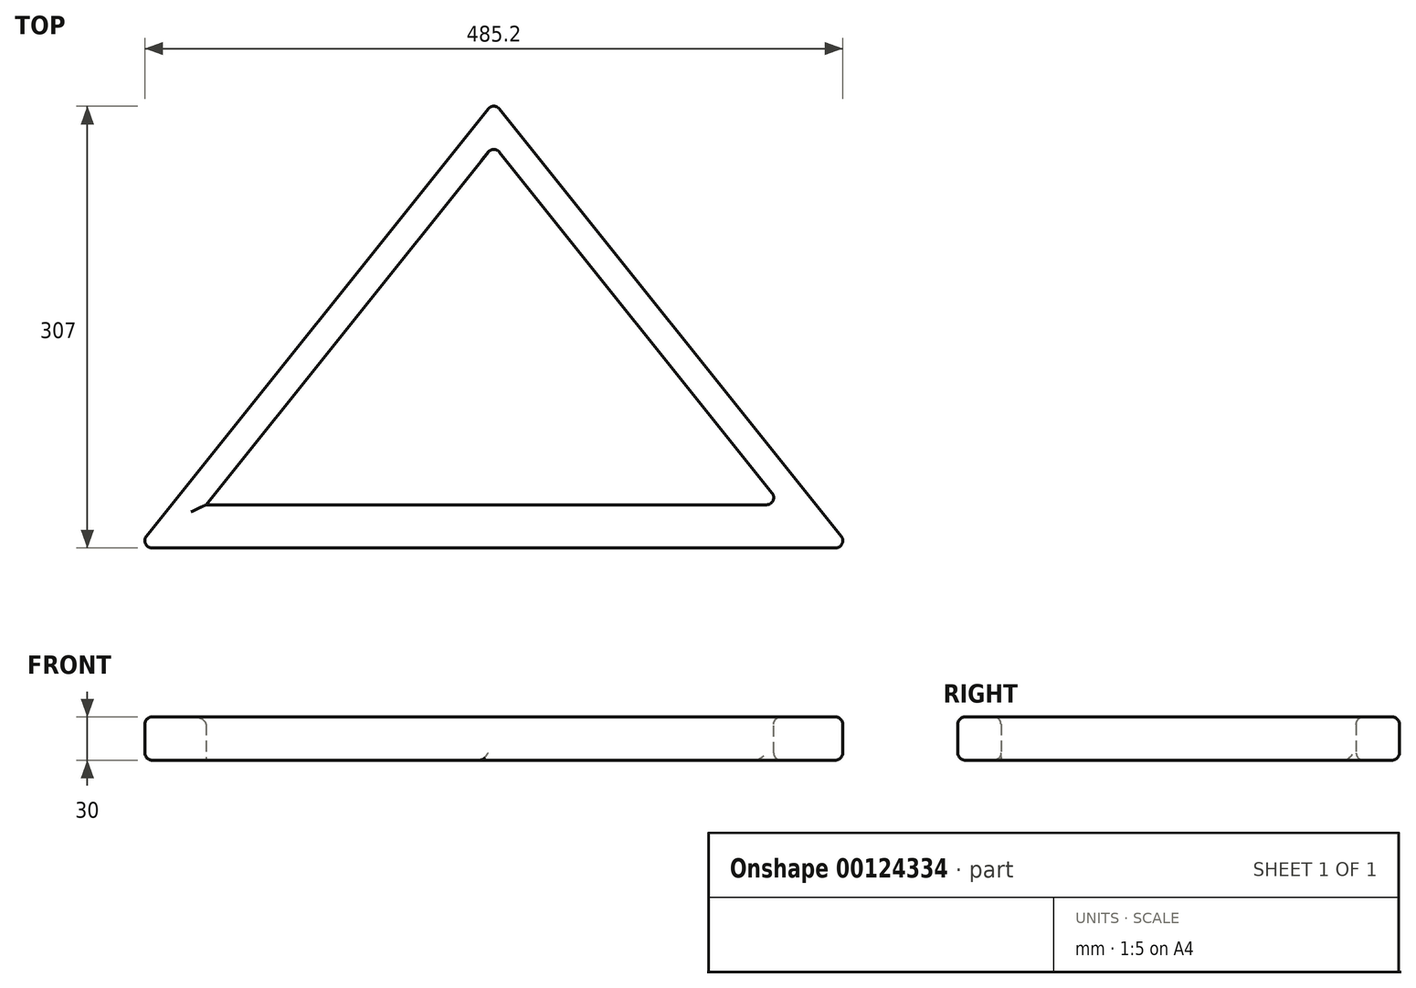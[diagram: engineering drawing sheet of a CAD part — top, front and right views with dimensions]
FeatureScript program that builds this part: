
annotation { "Feature Type Name" : "Feature", "Feature Type Description" : "" }
export const myFeature = defineFeature(function(context is Context, id is Id, definition is map)
    precondition{}
    {
        {
            var Q0;
            Q0=qCreatedBy(makeId("Top.planeOp"),FACE);
            var sketch = newSketch(context, id + "F0", { "sketchPlane" : qUnion([Q0])});
            skLineSegment(sketch, "E0", {"start": v(0, 0) * mm, "end": v(0, 250) * mm, "construction": true});
            skLineSegment(sketch, "E1", {"start": v(0, 0) * mm, "end": v(200, 0) * mm});
            skLineSegment(sketch, "E2", {"start": v(0, 0) * mm, "end": v(-200, 0) * mm});
            skLineSegment(sketch, "E3", {"start": v(-200, 0) * mm, "end": v(0, 250) * mm});
            skLineSegment(sketch, "E4", {"start": v(200, 0) * mm, "end": v(0, 250) * mm});
            skLineSegment(sketch, "E5", {"start": v(0, 0) * mm, "end": v(0, 280) * mm, "construction": true});
            skLineSegment(sketch, "E6", {"start": v(0, 0) * mm, "end": v(0, -30) * mm, "construction": true});
            skLineSegment(sketch, "E7", {"start": v(0, -30) * mm, "end": v(248, -30) * mm});
            skLineSegment(sketch, "E8", {"start": v(0, -30) * mm, "end": v(-248, -30) * mm});
            skLineSegment(sketch, "E9", {"start": v(-248, -30) * mm, "end": v(0, 280) * mm});
            skLineSegment(sketch, "E10", {"start": v(0, 280) * mm, "end": v(248, -30) * mm});
            skSolve(sketch);
        }
        {
            var Q0;
            Q0=makeQuery(id+"F0.imprint","IMPRINT",FACE,{"disambiguationData":[TD([[makeQuery(id+"F0.imprint","IMPRINT",EDGE,{"derivedFrom":sQuery(id+"F0.wireOp",EDGE,"E1")}),-1.0]])]});
            extrude(context, id + "F1", {"entities" : qUnion([Q0]), "depth" : 30 * mm});
        }
        {
            var Q0;
            Q0=makeQuery(id+"F1.opExtrude","SWEPT_FACE",FACE,{"disambiguationData":[OSD([sQuery(id+"F0.wireOp",EDGE,"E9")])]});
            var Q1;
            Q1=makeQuery(id+"F1.opExtrude","SWEPT_FACE",FACE,{"disambiguationData":[OSD([sQuery(id+"F0.wireOp",EDGE,"E10")])]});
            var Q2;
            Q2=makeQuery(id+"F1.opExtrude","SWEPT_FACE",FACE,{"disambiguationData":[OSD([sQuery(id+"F0.wireOp",EDGE,"E7"),sQuery(id+"F0.wireOp",EDGE,"E8")])]});
            var Q3;
            Q3=makeQuery(id+"F1.opExtrude","CAP_EDGE",EDGE,{"disambiguationData":[OSD([sQuery(id+"F0.wireOp",EDGE,"E1"),sQuery(id+"F0.wireOp",EDGE,"E2")])],"isStart":false});
            var Q4;
            Q4=makeQuery(id+"F1.opExtrude","CAP_EDGE",EDGE,{"disambiguationData":[OSD([sQuery(id+"F0.wireOp",EDGE,"E3")])],"isStart":false});
            var Q5;
            Q5=makeQuery(id+"F1.opExtrude","SWEPT_FACE",FACE,{"disambiguationData":[OSD([sQuery(id+"F0.wireOp",EDGE,"E4")])]});
            var Q6;
            Q6=makeQuery(id+"F1.opExtrude","CAP_FACE",FACE,{"disambiguationData":[OSD([sQuery(id+"F0.wireOp",EDGE,"E1"),sQuery(id+"F0.wireOp",EDGE,"E2"),sQuery(id+"F0.wireOp",EDGE,"E3"),sQuery(id+"F0.wireOp",EDGE,"E4"),sQuery(id+"F0.wireOp",EDGE,"E7"),sQuery(id+"F0.wireOp",EDGE,"E8"),sQuery(id+"F0.wireOp",EDGE,"E9"),sQuery(id+"F0.wireOp",EDGE,"E10")])],"isStart":false});
            fillet(context, id + "F2", {"entities" : qUnion([Q0, Q1, Q2, Q3, Q4, Q5, Q6]), "radius" : 5 * mm, "tangentPropagation" : true, "allowEdgeOverflow" : false});
        }
    });
